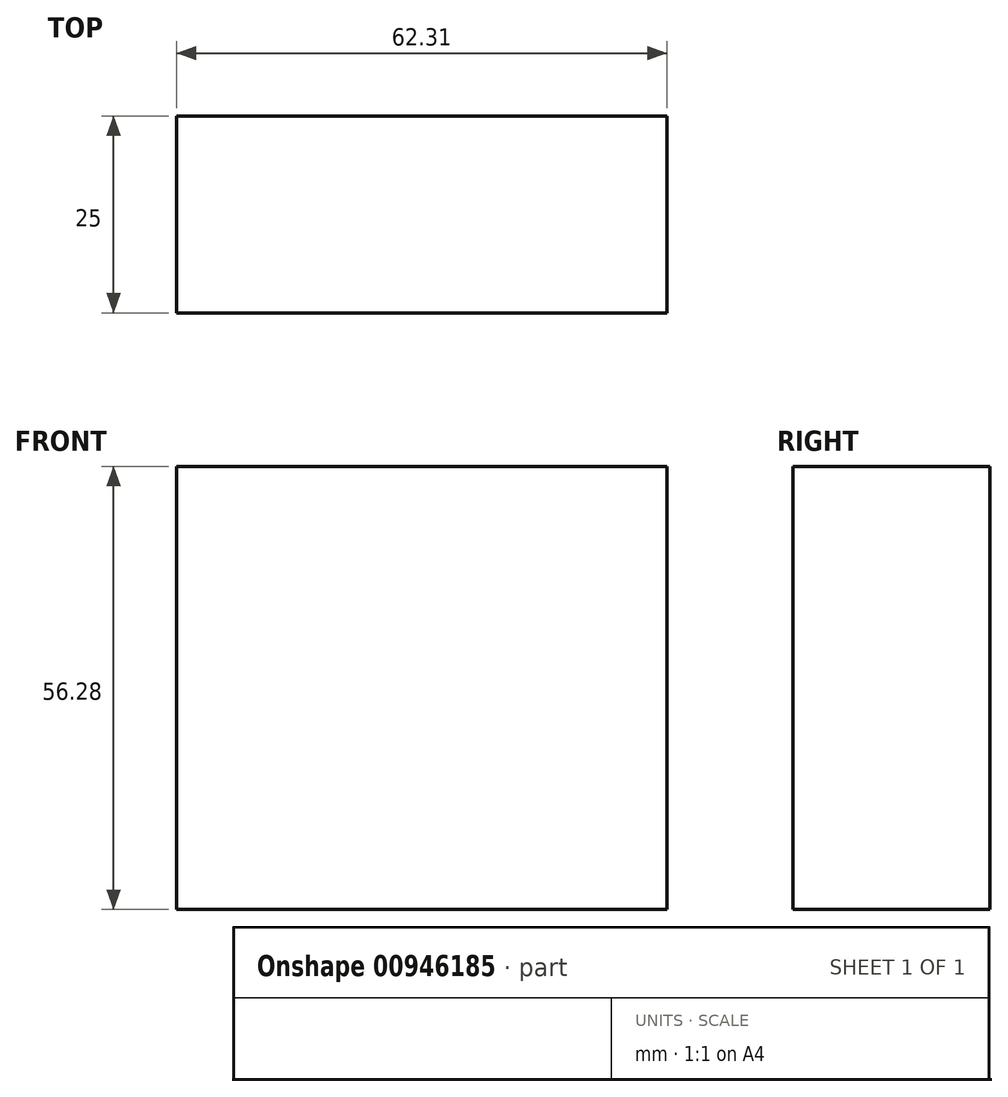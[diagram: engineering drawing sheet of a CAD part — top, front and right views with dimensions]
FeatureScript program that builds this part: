
annotation { "Feature Type Name" : "Feature", "Feature Type Description" : "" }
export const myFeature = defineFeature(function(context is Context, id is Id, definition is map)
    precondition{}
    {
        {
            var Q0;
            Q0=qCreatedBy(makeId("Front.planeOp"),FACE);
            var sketch = newSketch(context, id + "F0", { "sketchPlane" : qUnion([Q0])});
            skLineSegment(sketch, "E0.bottom", {"start": v(-102.72, 17.25) * mm, "end": v(-40.4, 17.25) * mm});
            skLineSegment(sketch, "E0.top", {"start": v(-102.72, 73.53) * mm, "end": v(-40.4, 73.53) * mm});
            skLineSegment(sketch, "E0.left", {"start": v(-102.72, 17.25) * mm, "end": v(-102.72, 73.53) * mm});
            skLineSegment(sketch, "E0.right", {"start": v(-40.4, 17.25) * mm, "end": v(-40.4, 73.53) * mm});
            skPoint(sketch, "E0.middle", {"position": v(-71.57, 45.39) * mm});
            skSolve(sketch);
        }
        {
            var Q0;
            Q0=makeQuery(id+"F0.imprint","IMPRINT",FACE,{"disambiguationData":[TD([[makeQuery(id+"F0.imprint","IMPRINT",EDGE,{"derivedFrom":sQuery(id+"F0.wireOp",EDGE,"E0.bottom")}),1.0]])]});
            extrude(context, id + "F1", {"entities" : qUnion([Q0]), "depth" : 25 * mm, "offsetDistance" : 25 * mm});
        }
    });
